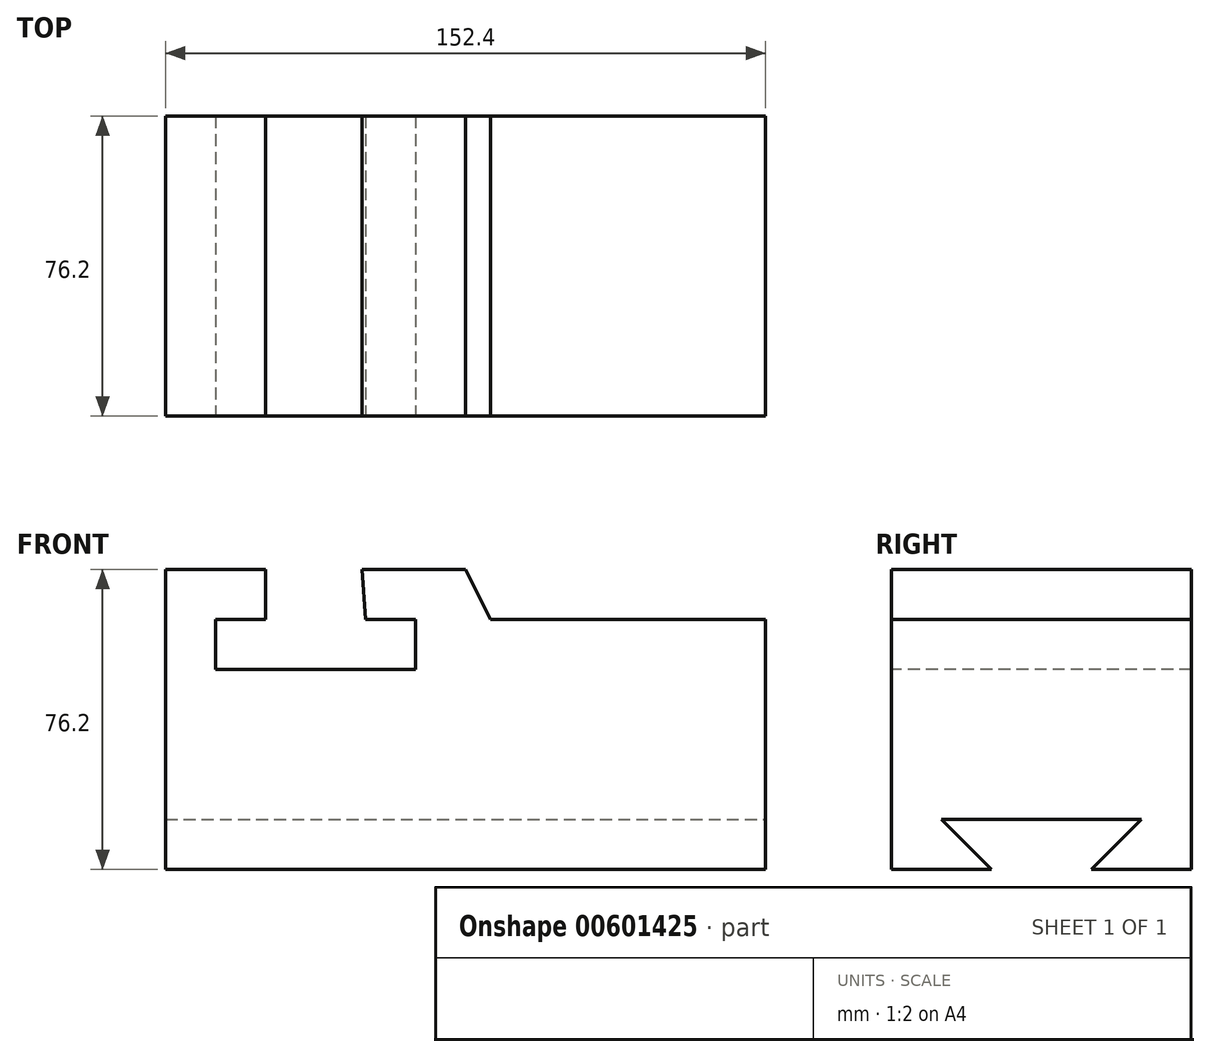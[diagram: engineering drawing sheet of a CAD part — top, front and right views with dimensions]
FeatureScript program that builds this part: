
annotation { "Feature Type Name" : "Feature", "Feature Type Description" : "" }
export const myFeature = defineFeature(function(context is Context, id is Id, definition is map)
    precondition{}
    {
        {
            var Q0;
            Q0=qCreatedBy(makeId("Front.planeOp"),FACE);
            var sketch = newSketch(context, id + "F0", { "sketchPlane" : qUnion([Q0])});
            skLineSegment(sketch, "E0", {"start": v(-49.9, -76.2) * mm, "end": v(102.5, -76.2) * mm});
            skLineSegment(sketch, "E1", {"start": v(102.5, -76.2) * mm, "end": v(102.5, 0) * mm});
            skLineSegment(sketch, "E2", {"start": v(102.5, 0) * mm, "end": v(-49.9, 0) * mm});
            skLineSegment(sketch, "E3", {"start": v(-49.9, 0) * mm, "end": v(-49.9, -76.2) * mm});
            skSolve(sketch);
        }
        {
            var Q0;
            Q0 = qSketchRegion(id + "F0", true);
            extrude(context, id + "F1", {"entities" : qUnion([Q0]), "depth" : 76.2 * mm, "offsetDistance" : 25.4 * mm});
        }
        {
            var Q0;
            Q0=makeQuery(id+"F1.opExtrude","CAP_FACE",FACE,{"disambiguationData":[OSD([sQuery(id+"F0.wireOp",EDGE,"E0"),sQuery(id+"F0.wireOp",EDGE,"E1"),sQuery(id+"F0.wireOp",EDGE,"E2"),sQuery(id+"F0.wireOp",EDGE,"E3")])],"isStart":false});
            var sketch = newSketch(context, id + "F2", { "sketchPlane" : qUnion([Q0])});
            skLineSegment(sketch, "E4", {"start": v(102.5, -76.2) * mm, "end": v(102.5, -12.7) * mm});
            skLineSegment(sketch, "E5", {"start": v(102.5, -12.7) * mm, "end": v(32.65, -12.7) * mm});
            skLineSegment(sketch, "E6", {"start": v(-49.9, 0) * mm, "end": v(-24.5, 0) * mm});
            skLineSegment(sketch, "E7", {"start": v(0.9, 0) * mm, "end": v(26.3, 0) * mm});
            skLineSegment(sketch, "E8", {"start": v(32.65, -12.7) * mm, "end": v(26.3, 0) * mm});
            skLineSegment(sketch, "E9", {"start": v(-24.5, 0) * mm, "end": v(-24.5, -12.7) * mm});
            skLineSegment(sketch, "E10", {"start": v(-24.5, -12.7) * mm, "end": v(-37.2, -12.7) * mm});
            skLineSegment(sketch, "E11", {"start": v(-37.2, -12.7) * mm, "end": v(-37.2, -25.4) * mm});
            skLineSegment(sketch, "E12", {"start": v(-37.2, -25.4) * mm, "end": v(13.6, -25.4) * mm});
            skLineSegment(sketch, "E13", {"start": v(13.6, -25.4) * mm, "end": v(13.6, -12.7) * mm});
            skLineSegment(sketch, "E14", {"start": v(13.6, -12.7) * mm, "end": v(0.9, -12.7) * mm});
            skLineSegment(sketch, "E15", {"start": v(0.9, -12.7) * mm, "end": v(0, 0) * mm});
            skSolve(sketch);
        }
        {
            var Q0;
            Q0 = qSketchRegion(id + "F2", true);
            var Q1;
            {var subQ0=sQuery(id+"F2.wireOp",EDGE,"E9");Q1=makeQuery(id+"F2.imprint","IMPRINT",FACE,{"disambiguationData":[TD([[makeQuery(id+"F2.imprint","IMPRINT",EDGE,{"derivedFrom":subQ0}),1.0]])]});}
            var Q2;
            {var subQ0=sQuery(id+"F2.wireOp",EDGE,"E5");Q2=makeQuery(id+"F2.imprint","IMPRINT",FACE,{"disambiguationData":[TD([[makeQuery(id+"F2.imprint","IMPRINT",EDGE,{"derivedFrom":subQ0}),-1.0]])]});}
            extrude(context, id + "F3", {"entities" : qUnion([Q0, Q1, Q2]), "operationType" : NewBodyOperationType.REMOVE, "oppositeDirection" : true, "depth" : 76.2 * mm, "offsetDistance" : 25.4 * mm});
        }
        {
            var Q0;
            Q0=makeQuery(id+"F1.opExtrude","SWEPT_FACE",FACE,{"disambiguationData":[OSD([sQuery(id+"F0.wireOp",EDGE,"E1")])]});
            var sketch = newSketch(context, id + "F4", { "sketchPlane" : qUnion([Q0])});
            skLineSegment(sketch, "E16", {"start": v(0, -76.2) * mm, "end": v(-25.4, -76.2) * mm});
            skLineSegment(sketch, "E17", {"start": v(-76.2, -76.2) * mm, "end": v(-50.8, -76.2) * mm});
            skLineSegment(sketch, "E18", {"start": v(0, -76.2) * mm, "end": v(0, -63.5) * mm});
            skLineSegment(sketch, "E19", {"start": v(0, -63.5) * mm, "end": v(-12.7, -63.5) * mm});
            skLineSegment(sketch, "E20", {"start": v(-12.7, -63.5) * mm, "end": v(-25.4, -76.2) * mm});
            skLineSegment(sketch, "E21", {"start": v(-76.2, -76.2) * mm, "end": v(-76.2, -63.5) * mm});
            skLineSegment(sketch, "E22", {"start": v(-76.2, -63.5) * mm, "end": v(-63.5, -63.5) * mm});
            skLineSegment(sketch, "E23", {"start": v(-63.5, -63.5) * mm, "end": v(-50.8, -76.2) * mm});
            skLineSegment(sketch, "E24", {"start": v(-63.5, -63.5) * mm, "end": v(-12.7, -63.5) * mm});
            skSolve(sketch);
        }
        {
            var Q0;
            {var subQ0=sQuery(id+"F4.wireOp",EDGE,"E20");Q0=makeQuery(id+"F4.imprint","IMPRINT",FACE,{"disambiguationData":[TD([[makeQuery(id+"F4.imprint","IMPRINT",EDGE,{"derivedFrom":subQ0}),-1.0]])]});}
            extrude(context, id + "F5", {"entities" : qUnion([Q0]), "operationType" : NewBodyOperationType.REMOVE, "endBound" : BoundingType.UP_TO_NEXT, "oppositeDirection" : true, "depth" : 25.4 * mm, "offsetDistance" : 25.4 * mm});
        }
    });
